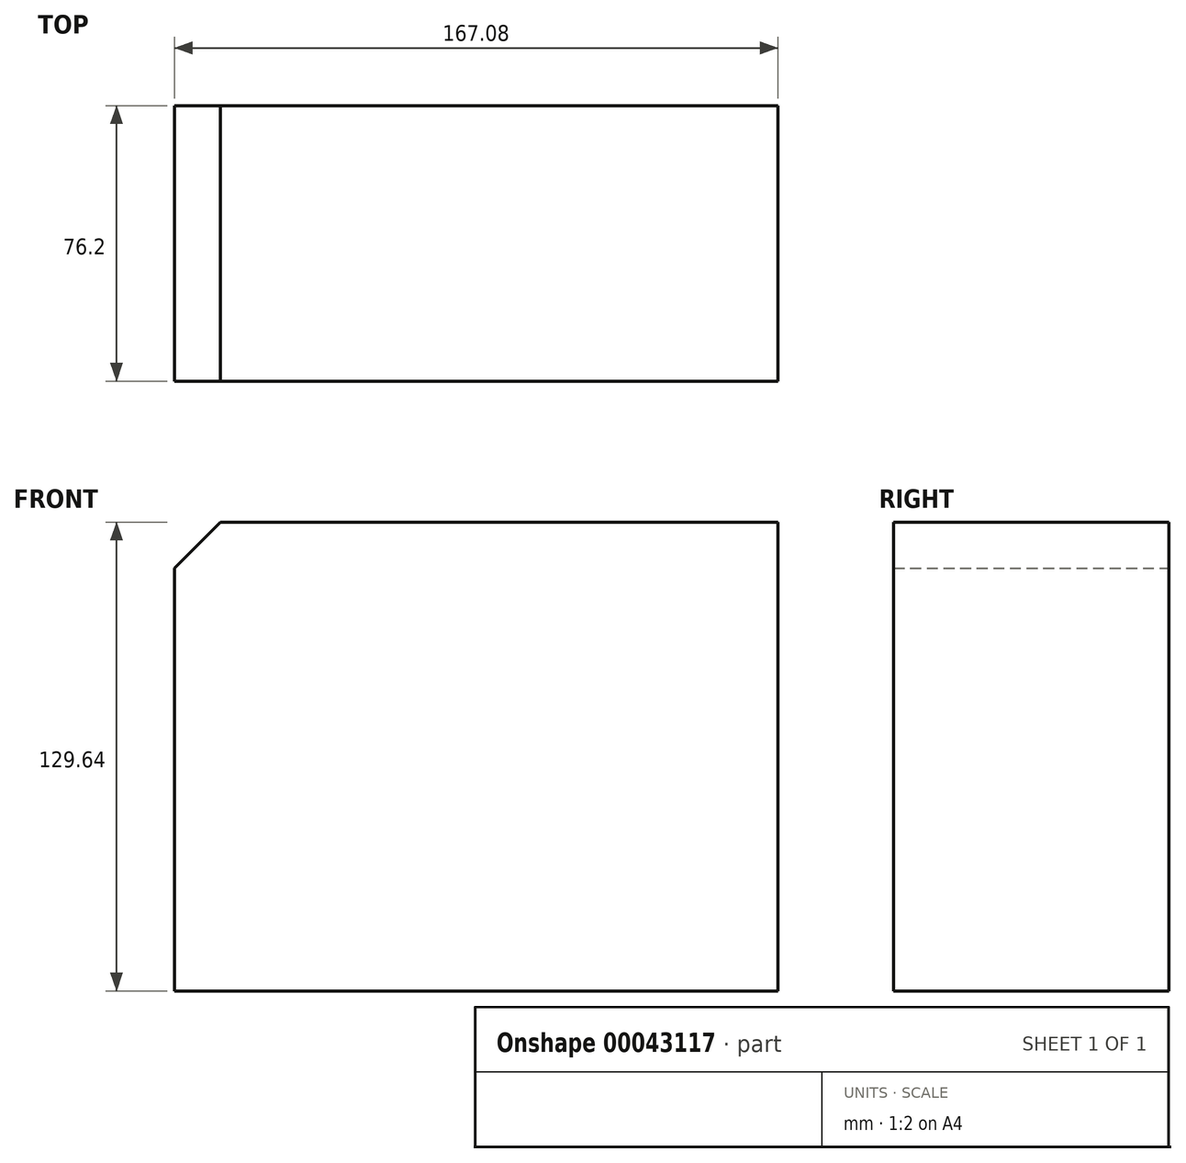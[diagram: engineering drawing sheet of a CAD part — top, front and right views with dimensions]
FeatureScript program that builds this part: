
annotation { "Feature Type Name" : "Feature", "Feature Type Description" : "" }
export const myFeature = defineFeature(function(context is Context, id is Id, definition is map)
    precondition{}
    {
        {
            var Q0;
            Q0=qCreatedBy(makeId("Front.planeOp"),FACE);
            var sketch = newSketch(context, id + "F0", { "sketchPlane" : qUnion([Q0])});
            skLineSegment(sketch, "E0.bottom", {"start": v(-43.13, 84.46) * mm, "end": v(123.95, 84.46) * mm});
            skLineSegment(sketch, "E0.top", {"start": v(-43.13, -45.18) * mm, "end": v(123.95, -45.18) * mm});
            skLineSegment(sketch, "E0.left", {"start": v(-43.13, 84.46) * mm, "end": v(-43.13, -45.18) * mm});
            skLineSegment(sketch, "E0.right", {"start": v(123.95, 84.46) * mm, "end": v(123.95, -45.18) * mm});
            skSolve(sketch);
        }
        {
            var Q0;
            Q0 = qSketchRegion(id + "F0", true);
            extrude(context, id + "F1", {"entities" : qUnion([Q0]), "depth" : 76.2 * mm});
        }
        {
            var Q0;
            Q0=makeQuery(id+"F1.opExtrude","SWEPT_EDGE",EDGE,{"disambiguationData":[OSD([sQuery(id+"F0.wireOp",EDGE,"E0.bottom"),sQuery(id+"F0.wireOp",EDGE,"E0.left")])]});
            chamfer(context, id + "F2", {"entities" : qUnion([Q0]), "width" : 12.7 * mm, "tangentPropagation" : true});
        }
    });
